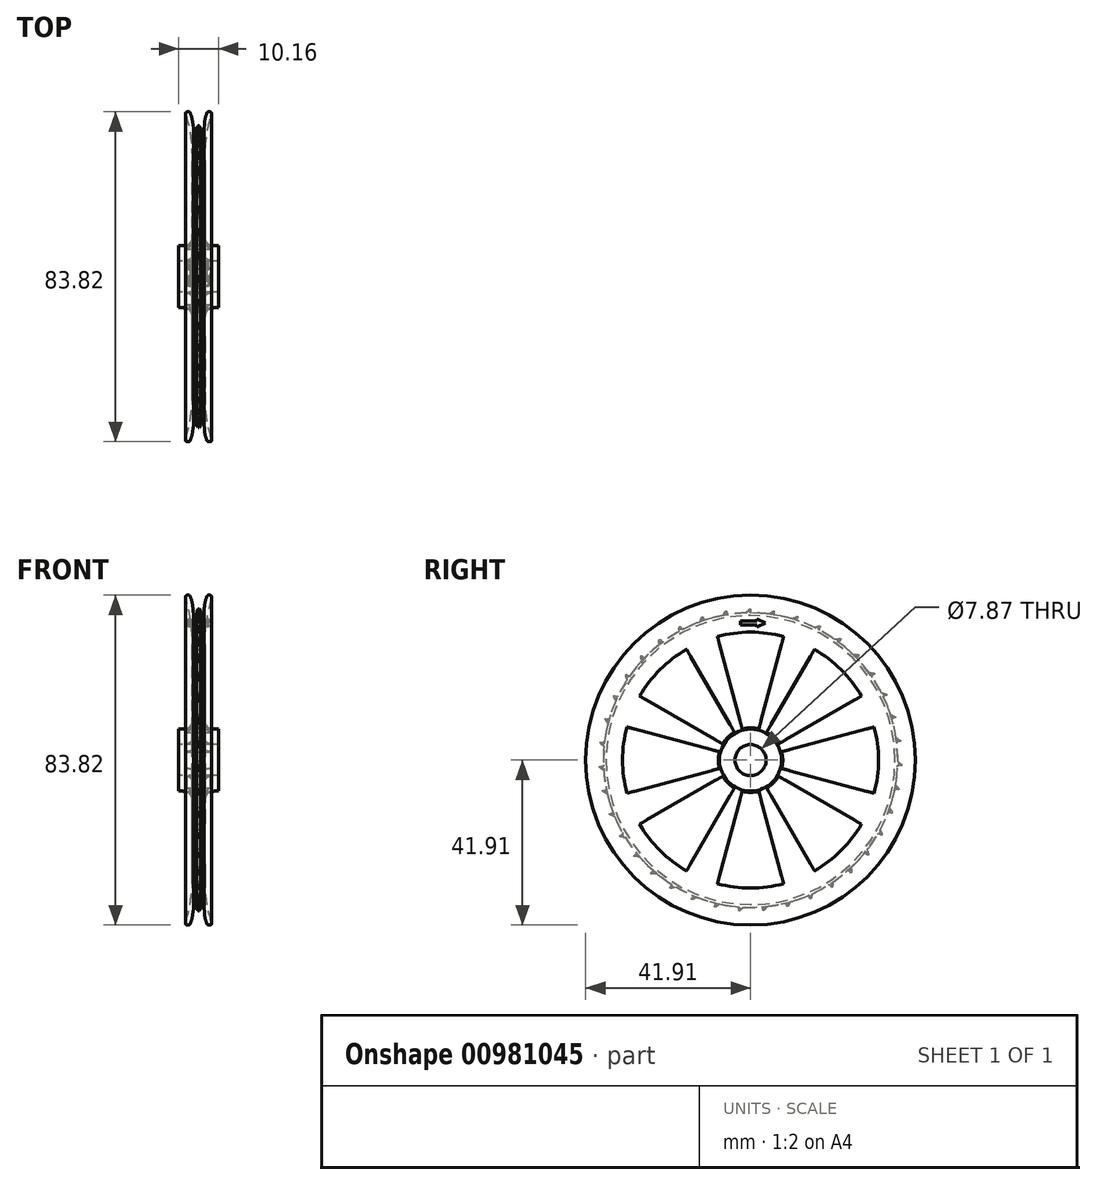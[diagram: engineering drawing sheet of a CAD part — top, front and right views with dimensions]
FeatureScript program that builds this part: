
annotation { "Feature Type Name" : "Feature", "Feature Type Description" : "" }
export const myFeature = defineFeature(function(context is Context, id is Id, definition is map)
    precondition{}
    {
        {
            var Q0;
            Q0=qCreatedBy(makeId("Front.planeOp"),FACE);
            var sketch = newSketch(context, id + "F0", { "sketchPlane" : qUnion([Q0])});
            skLineSegment(sketch, "E0", {"start": v(0, 0) * mm, "end": v(19.05, 0) * mm, "construction": true});
            skLineSegment(sketch, "E1", {"start": v(-5.08, 3.94) * mm, "end": v(0, 3.94) * mm});
            skLineSegment(sketch, "E2", {"start": v(-4.09, 45.93) * mm, "end": v(-2.38, 42.25) * mm});
            skLineSegment(sketch, "E3", {"start": v(0, 45.68) * mm, "end": v(0, -5.83) * mm, "construction": true});
            skPoint(sketch, "E4.visualSharp", {"position": v(0, 36.7) * mm});
            skLineSegment(sketch, "E5", {"start": v(-1.65, 10.41) * mm, "end": v(-1.65, 30.48) * mm});
            skLineSegment(sketch, "E6.trimOffspring", {"start": v(-5.08, 7.87) * mm, "end": v(-5.08, 3.94) * mm});
            skPoint(sketch, "E7.visualSharp", {"position": v(-1.65, 7.87) * mm});
            skLineSegment(sketch, "E8", {"start": v(-1.4, 38.1) * mm, "end": v(-1.46, 38.85) * mm});
            skLineSegment(sketch, "E9", {"start": v(-5.08, 7.87) * mm, "end": v(-4.2, 7.87) * mm});
            skArc(sketch, "E10", {"start": v(-4.09, 45.93) * mm, "mid": v(-4.74, 46.17) * mm, "end": v(-4.98, 45.51) * mm});
            skPoint(sketch, "E11.visualSharp", {"position": v(-1.65, 37.42) * mm});
            skArc(sketch, "E11.filletArc", {"start": v(-1.65, 30.48) * mm, "mid": v(-2.5, 38.18) * mm, "end": v(-4.98, 45.51) * mm});
            skPoint(sketch, "E12.visualSharp", {"position": v(-1.62, 40.63) * mm});
            skArc(sketch, "E12.filletArc", {"start": v(-1.46, 38.85) * mm, "mid": v(-1.77, 40.59) * mm, "end": v(-2.38, 42.25) * mm});
            skPoint(sketch, "E13.visualSharp", {"position": v(-1.4, 38.1) * mm});
            skArc(sketch, "E14.filletArc", {"start": v(-4.2, 7.87) * mm, "mid": v(-2.4, 8.62) * mm, "end": v(-1.65, 10.41) * mm});
            skLineSegment(sketch, "E15.MirrorCS", {"start": v(1.4, 38.1) * mm, "end": v(1.46, 38.85) * mm});
            skLineSegment(sketch, "E16.MirrorCS", {"start": v(5.08, 7.87) * mm, "end": v(4.2, 7.87) * mm});
            skArc(sketch, "E17.MirrorCS", {"start": v(1.46, 38.85) * mm, "mid": v(1.77, 40.59) * mm, "end": v(2.38, 42.25) * mm});
            skArc(sketch, "E18.MirrorCS", {"start": v(4.09, 45.93) * mm, "mid": v(4.74, 46.17) * mm, "end": v(4.98, 45.51) * mm});
            skLineSegment(sketch, "E19.MirrorCS", {"start": v(4.09, 45.93) * mm, "end": v(2.38, 42.25) * mm});
            skArc(sketch, "E20.MirrorCS", {"start": v(4.2, 7.87) * mm, "mid": v(2.4, 8.62) * mm, "end": v(1.65, 10.41) * mm});
            skPoint(sketch, "E21.MirrorP", {"position": v(1.65, 7.87) * mm});
            skPoint(sketch, "E22.MirrorP", {"position": v(1.4, 38.1) * mm});
            skPoint(sketch, "E23.MirrorP", {"position": v(1.65, 37.42) * mm});
            skLineSegment(sketch, "E24.MirrorCS", {"start": v(1.65, 10.41) * mm, "end": v(1.65, 30.48) * mm});
            skLineSegment(sketch, "E25.MirrorCS", {"start": v(5.08, 7.87) * mm, "end": v(5.08, 3.94) * mm});
            skPoint(sketch, "E26.MirrorP", {"position": v(1.62, 40.63) * mm});
            skLineSegment(sketch, "E27.MirrorCS", {"start": v(5.08, 3.94) * mm, "end": v(0, 3.94) * mm});
            skArc(sketch, "E28.MirrorCS", {"start": v(1.65, 30.48) * mm, "mid": v(2.5, 38.18) * mm, "end": v(4.98, 45.51) * mm});
            skLineSegment(sketch, "E29", {"start": v(-0.7, 37.4) * mm, "end": v(0.7, 37.4) * mm});
            skLineSegment(sketch, "E30", {"start": v(-0.7, 37.4) * mm, "end": v(-1.34, 37.4) * mm});
            skLineSegment(sketch, "E31", {"start": v(-1.4, 38.1) * mm, "end": v(-1.34, 37.4) * mm});
            skLineSegment(sketch, "E32.MirrorCS", {"start": v(1.4, 38.1) * mm, "end": v(1.34, 37.4) * mm});
            skLineSegment(sketch, "E33.MirrorCS", {"start": v(0.7, 37.4) * mm, "end": v(1.34, 37.4) * mm});
            skSolve(sketch);
        }
        {
            var Q0;
            Q0=qSketchRegion(id+"F0",true);
            var Q1;
            Q1=sQuery(id+"F0.wireOp",EDGE,"E0");
            revolve(context, id + "F1", {"surfaceOperationType" : NewSurfaceOperationType.NEW, "entities" : qUnion([Q0]), "axis" : qUnion([Q1]), "revolveType" : RevolveType.FULL});
        }
        {
            var Q0;
            Q0=qCreatedBy(makeId("Right.planeOp"),FACE);
            var sketch = newSketch(context, id + "F2", { "sketchPlane" : qUnion([Q0])});
            skArc(sketch, "E34", {"start": v(0, 32.51) * mm, "mid": v(-4.24, 32.23) * mm, "end": v(-8.41, 31.4) * mm});
            skArc(sketch, "E35", {"start": v(0, 8.18) * mm, "mid": v(-1.07, 8.11) * mm, "end": v(-2.12, 7.9) * mm});
            skLineSegment(sketch, "E36", {"start": v(0, 35.5) * mm, "end": v(0, 4.54) * mm, "construction": true});
            skLineSegment(sketch, "E37", {"start": v(-2.12, 7.9) * mm, "end": v(-8.41, 31.4) * mm});
            skArc(sketch, "E38.MirrorCS", {"start": v(0, 32.51) * mm, "mid": v(4.24, 32.23) * mm, "end": v(8.41, 31.4) * mm});
            skLineSegment(sketch, "E39.MirrorCS", {"start": v(2.12, 7.9) * mm, "end": v(8.41, 31.4) * mm});
            skArc(sketch, "E40.MirrorCS", {"start": v(0, 8.18) * mm, "mid": v(1.07, 8.11) * mm, "end": v(2.12, 7.9) * mm});
            skLineSegment(sketch, "E41.1.0", {"start": v(-7.08, 4.1) * mm, "end": v(-28.16, 16.26) * mm});
            skArc(sketch, "E41.1.1", {"start": v(-22.99, 22.99) * mm, "mid": v(-25.8, 19.8) * mm, "end": v(-28.16, 16.26) * mm});
            skArc(sketch, "E41.1.2", {"start": v(-5.78, 5.78) * mm, "mid": v(-6.5, 4.98) * mm, "end": v(-7.08, 4.1) * mm});
            skArc(sketch, "E41.1.3", {"start": v(-5.78, 5.78) * mm, "mid": v(-4.98, 6.5) * mm, "end": v(-4.1, 7.08) * mm});
            skLineSegment(sketch, "E41.1.4", {"start": v(-4.1, 7.08) * mm, "end": v(-16.26, 28.16) * mm});
            skArc(sketch, "E41.1.5", {"start": v(-22.99, 22.99) * mm, "mid": v(-19.8, 25.8) * mm, "end": v(-16.26, 28.16) * mm});
            skLineSegment(sketch, "E41.2.0", {"start": v(-7.9, -2.12) * mm, "end": v(-31.4, -8.41) * mm});
            skArc(sketch, "E41.2.1", {"start": v(-32.51, 0) * mm, "mid": v(-32.23, -4.24) * mm, "end": v(-31.4, -8.41) * mm});
            skArc(sketch, "E41.2.2", {"start": v(-8.18, 0) * mm, "mid": v(-8.11, -1.07) * mm, "end": v(-7.9, -2.12) * mm});
            skArc(sketch, "E41.2.3", {"start": v(-8.18, 0) * mm, "mid": v(-8.11, 1.07) * mm, "end": v(-7.9, 2.12) * mm});
            skLineSegment(sketch, "E41.2.4", {"start": v(-7.9, 2.12) * mm, "end": v(-31.4, 8.41) * mm});
            skArc(sketch, "E41.2.5", {"start": v(-32.51, 0) * mm, "mid": v(-32.23, 4.24) * mm, "end": v(-31.4, 8.41) * mm});
            skLineSegment(sketch, "E42.1.3.0", {"start": v(-4.1, -7.08) * mm, "end": v(-16.26, -28.16) * mm});
            skArc(sketch, "E42.3.3.0", {"start": v(-22.99, -22.99) * mm, "mid": v(-19.8, -25.8) * mm, "end": v(-16.26, -28.16) * mm});
            skArc(sketch, "E42.7.3.0", {"start": v(-5.78, -5.78) * mm, "mid": v(-4.98, -6.5) * mm, "end": v(-4.1, -7.08) * mm});
            skArc(sketch, "E42.11.3.0", {"start": v(-5.78, -5.78) * mm, "mid": v(-6.5, -4.98) * mm, "end": v(-7.08, -4.1) * mm});
            skLineSegment(sketch, "E42.15.3.0", {"start": v(-7.08, -4.1) * mm, "end": v(-28.16, -16.26) * mm});
            skArc(sketch, "E42.18.3.0", {"start": v(-22.99, -22.99) * mm, "mid": v(-25.8, -19.8) * mm, "end": v(-28.16, -16.26) * mm});
            skLineSegment(sketch, "E42.1.4.0", {"start": v(2.12, -7.9) * mm, "end": v(8.41, -31.4) * mm});
            skArc(sketch, "E42.3.4.0", {"start": v(0, -32.51) * mm, "mid": v(4.24, -32.23) * mm, "end": v(8.41, -31.4) * mm});
            skArc(sketch, "E42.7.4.0", {"start": v(0, -8.18) * mm, "mid": v(1.07, -8.11) * mm, "end": v(2.12, -7.9) * mm});
            skArc(sketch, "E42.11.4.0", {"start": v(0, -8.18) * mm, "mid": v(-1.07, -8.11) * mm, "end": v(-2.12, -7.9) * mm});
            skLineSegment(sketch, "E42.15.4.0", {"start": v(-2.12, -7.9) * mm, "end": v(-8.41, -31.4) * mm});
            skArc(sketch, "E42.18.4.0", {"start": v(0, -32.51) * mm, "mid": v(-4.24, -32.23) * mm, "end": v(-8.41, -31.4) * mm});
            skLineSegment(sketch, "E42.1.5.0", {"start": v(7.08, -4.1) * mm, "end": v(28.16, -16.26) * mm});
            skArc(sketch, "E42.3.5.0", {"start": v(22.99, -22.99) * mm, "mid": v(25.8, -19.8) * mm, "end": v(28.16, -16.26) * mm});
            skArc(sketch, "E42.7.5.0", {"start": v(5.78, -5.78) * mm, "mid": v(6.5, -4.98) * mm, "end": v(7.08, -4.1) * mm});
            skArc(sketch, "E42.11.5.0", {"start": v(5.78, -5.78) * mm, "mid": v(4.98, -6.5) * mm, "end": v(4.1, -7.08) * mm});
            skLineSegment(sketch, "E42.15.5.0", {"start": v(4.1, -7.08) * mm, "end": v(16.26, -28.16) * mm});
            skArc(sketch, "E42.18.5.0", {"start": v(22.99, -22.99) * mm, "mid": v(19.8, -25.8) * mm, "end": v(16.26, -28.16) * mm});
            skLineSegment(sketch, "E42.1.6.0", {"start": v(7.9, 2.12) * mm, "end": v(31.4, 8.41) * mm});
            skArc(sketch, "E42.3.6.0", {"start": v(32.51, 0) * mm, "mid": v(32.23, 4.24) * mm, "end": v(31.4, 8.41) * mm});
            skArc(sketch, "E42.7.6.0", {"start": v(8.18, 0) * mm, "mid": v(8.11, 1.07) * mm, "end": v(7.9, 2.12) * mm});
            skArc(sketch, "E42.11.6.0", {"start": v(8.18, 0) * mm, "mid": v(8.11, -1.07) * mm, "end": v(7.9, -2.12) * mm});
            skLineSegment(sketch, "E42.15.6.0", {"start": v(7.9, -2.12) * mm, "end": v(31.4, -8.41) * mm});
            skArc(sketch, "E42.18.6.0", {"start": v(32.51, 0) * mm, "mid": v(32.23, -4.24) * mm, "end": v(31.4, -8.41) * mm});
            skLineSegment(sketch, "E42.1.7.0", {"start": v(4.1, 7.08) * mm, "end": v(16.26, 28.16) * mm});
            skArc(sketch, "E42.3.7.0", {"start": v(22.99, 22.99) * mm, "mid": v(19.8, 25.8) * mm, "end": v(16.26, 28.16) * mm});
            skArc(sketch, "E42.7.7.0", {"start": v(5.78, 5.78) * mm, "mid": v(4.98, 6.5) * mm, "end": v(4.1, 7.08) * mm});
            skArc(sketch, "E42.11.7.0", {"start": v(5.78, 5.78) * mm, "mid": v(6.5, 4.98) * mm, "end": v(7.08, 4.1) * mm});
            skLineSegment(sketch, "E42.15.7.0", {"start": v(7.08, 4.1) * mm, "end": v(28.16, 16.26) * mm});
            skArc(sketch, "E42.18.7.0", {"start": v(22.99, 22.99) * mm, "mid": v(25.8, 19.8) * mm, "end": v(28.16, 16.26) * mm});
            skSolve(sketch);
        }
        {
            var Q0;
            Q0=qSketchRegion(id+"F2",true);
            extrude(context, id + "F3", {"entities" : qUnion([Q0]), "operationType" : NewBodyOperationType.REMOVE, "endBound" : BoundingType.SYMMETRIC, "oppositeDirection" : true, "depth" : 25.4 * mm, "offsetDistance" : 25.4 * mm});
        }
        {
            var Q0;
            Q0=qCreatedBy(makeId("Top.planeOp"),FACE);
            var sketch = newSketch(context, id + "F4", { "sketchPlane" : qUnion([Q0])});
            skLineSegment(sketch, "E43", {"start": v(0, 0) * mm, "end": v(21.6, 0) * mm, "construction": true});
            skSolve(sketch);
        }
        {
            var Q0;
            Q0=qCreatedBy(makeId("Right.planeOp"),FACE);
            var sketch = newSketch(context, id + "F7", { "sketchPlane" : qUnion([Q0])});
            skLineSegment(sketch, "E44", {"start": v(0, 38.35) * mm, "end": v(0, 36.32) * mm});
            skLineSegment(sketch, "E45", {"start": v(0, 36.32) * mm, "end": v(-1.96, 36.32) * mm});
            skLineSegment(sketch, "E46", {"start": v(-1.96, 36.32) * mm, "end": v(-0.25, 38.35) * mm});
            skLineSegment(sketch, "E47", {"start": v(-0.25, 38.35) * mm, "end": v(0, 38.35) * mm});
            skLineSegment(sketch, "E48.1.0", {"start": v(-6.16, 37.86) * mm, "end": v(-5.83, 35.85) * mm});
            skLineSegment(sketch, "E48.1.1", {"start": v(-7.76, 35.54) * mm, "end": v(-6.4, 37.82) * mm});
            skLineSegment(sketch, "E48.1.2", {"start": v(-5.83, 35.85) * mm, "end": v(-7.76, 35.54) * mm});
            skLineSegment(sketch, "E48.1.3", {"start": v(-6.4, 37.82) * mm, "end": v(-6.16, 37.86) * mm});
            skLineSegment(sketch, "E48.2.0", {"start": v(-12.15, 36.38) * mm, "end": v(-11.5, 34.45) * mm});
            skLineSegment(sketch, "E48.2.1", {"start": v(-13.37, 33.83) * mm, "end": v(-12.4, 36.3) * mm});
            skLineSegment(sketch, "E48.2.2", {"start": v(-11.5, 34.45) * mm, "end": v(-13.37, 33.83) * mm});
            skLineSegment(sketch, "E48.2.3", {"start": v(-12.4, 36.3) * mm, "end": v(-12.15, 36.38) * mm});
            skLineSegment(sketch, "E48.3.0", {"start": v(-17.83, 33.96) * mm, "end": v(-16.89, 32.16) * mm});
            skLineSegment(sketch, "E48.3.1", {"start": v(-18.62, 31.25) * mm, "end": v(-18.06, 33.84) * mm});
            skLineSegment(sketch, "E48.3.2", {"start": v(-16.89, 32.16) * mm, "end": v(-18.62, 31.25) * mm});
            skLineSegment(sketch, "E48.3.3", {"start": v(-18.06, 33.84) * mm, "end": v(-17.83, 33.96) * mm});
            skLineSegment(sketch, "E48.4.0", {"start": v(-23.05, 30.65) * mm, "end": v(-21.83, 29.03) * mm});
            skLineSegment(sketch, "E48.4.1", {"start": v(-23.4, 27.85) * mm, "end": v(-23.26, 30.5) * mm});
            skLineSegment(sketch, "E48.4.2", {"start": v(-21.83, 29.03) * mm, "end": v(-23.4, 27.85) * mm});
            skLineSegment(sketch, "E48.4.3", {"start": v(-23.26, 30.5) * mm, "end": v(-23.05, 30.65) * mm});
            skLineSegment(sketch, "E48.5.0", {"start": v(-27.68, 26.55) * mm, "end": v(-26.2, 25.15) * mm});
            skLineSegment(sketch, "E48.5.1", {"start": v(-27.57, 23.73) * mm, "end": v(-27.85, 26.37) * mm});
            skLineSegment(sketch, "E48.5.2", {"start": v(-26.2, 25.15) * mm, "end": v(-27.57, 23.73) * mm});
            skLineSegment(sketch, "E48.5.3", {"start": v(-27.85, 26.37) * mm, "end": v(-27.68, 26.55) * mm});
            skLineSegment(sketch, "E48.6.0", {"start": v(-31.58, 21.77) * mm, "end": v(-29.9, 20.61) * mm});
            skLineSegment(sketch, "E48.6.1", {"start": v(-31.02, 19) * mm, "end": v(-31.72, 21.56) * mm});
            skLineSegment(sketch, "E48.6.2", {"start": v(-29.9, 20.61) * mm, "end": v(-31.02, 19) * mm});
            skLineSegment(sketch, "E48.6.3", {"start": v(-31.72, 21.56) * mm, "end": v(-31.58, 21.77) * mm});
            skLineSegment(sketch, "E48.7.0", {"start": v(-34.66, 16.42) * mm, "end": v(-32.83, 15.55) * mm});
            skLineSegment(sketch, "E48.7.1", {"start": v(-33.67, 13.78) * mm, "end": v(-34.77, 16.19) * mm});
            skLineSegment(sketch, "E48.7.2", {"start": v(-32.83, 15.55) * mm, "end": v(-33.67, 13.78) * mm});
            skLineSegment(sketch, "E48.7.3", {"start": v(-34.77, 16.19) * mm, "end": v(-34.66, 16.42) * mm});
            skLineSegment(sketch, "E48.8.0", {"start": v(-36.85, 10.64) * mm, "end": v(-34.9, 10.08) * mm});
            skLineSegment(sketch, "E48.8.1", {"start": v(-35.44, 8.2) * mm, "end": v(-36.92, 10.4) * mm});
            skLineSegment(sketch, "E48.8.2", {"start": v(-34.9, 10.08) * mm, "end": v(-35.44, 8.2) * mm});
            skLineSegment(sketch, "E48.8.3", {"start": v(-36.92, 10.4) * mm, "end": v(-36.85, 10.64) * mm});
            skLineSegment(sketch, "E48.9.0", {"start": v(-38.08, 4.59) * mm, "end": v(-36.06, 4.34) * mm});
            skLineSegment(sketch, "E48.9.1", {"start": v(-36.3, 2.4) * mm, "end": v(-38.1, 4.33) * mm});
            skLineSegment(sketch, "E48.9.2", {"start": v(-36.06, 4.34) * mm, "end": v(-36.3, 2.4) * mm});
            skLineSegment(sketch, "E48.9.3", {"start": v(-38.1, 4.33) * mm, "end": v(-38.08, 4.59) * mm});
            skLineSegment(sketch, "E48.10.0", {"start": v(-38.32, -1.58) * mm, "end": v(-36.3, -1.5) * mm});
            skLineSegment(sketch, "E48.10.1", {"start": v(-36.21, -3.46) * mm, "end": v(-38.31, -1.84) * mm});
            skLineSegment(sketch, "E48.10.2", {"start": v(-36.3, -1.5) * mm, "end": v(-36.21, -3.46) * mm});
            skLineSegment(sketch, "E48.10.3", {"start": v(-38.31, -1.84) * mm, "end": v(-38.32, -1.58) * mm});
            skLineSegment(sketch, "E48.11.0", {"start": v(-37.57, -7.72) * mm, "end": v(-35.58, -7.3) * mm});
            skLineSegment(sketch, "E48.11.1", {"start": v(-35.19, -9.23) * mm, "end": v(-37.52, -7.96) * mm});
            skLineSegment(sketch, "E48.11.2", {"start": v(-35.58, -7.3) * mm, "end": v(-35.19, -9.23) * mm});
            skLineSegment(sketch, "E48.11.3", {"start": v(-37.52, -7.96) * mm, "end": v(-37.57, -7.72) * mm});
            skLineSegment(sketch, "E48.12.0", {"start": v(-35.84, -13.65) * mm, "end": v(-33.95, -12.92) * mm});
            skLineSegment(sketch, "E48.12.1", {"start": v(-33.25, -14.75) * mm, "end": v(-35.75, -13.88) * mm});
            skLineSegment(sketch, "E48.12.2", {"start": v(-33.95, -12.92) * mm, "end": v(-33.25, -14.75) * mm});
            skLineSegment(sketch, "E48.12.3", {"start": v(-35.75, -13.88) * mm, "end": v(-35.84, -13.65) * mm});
            skLineSegment(sketch, "E48.13.0", {"start": v(-33.19, -19.22) * mm, "end": v(-31.43, -18.2) * mm});
            skLineSegment(sketch, "E48.13.1", {"start": v(-30.45, -19.9) * mm, "end": v(-33.06, -19.44) * mm});
            skLineSegment(sketch, "E48.13.2", {"start": v(-31.43, -18.2) * mm, "end": v(-30.45, -19.9) * mm});
            skLineSegment(sketch, "E48.13.3", {"start": v(-33.06, -19.44) * mm, "end": v(-33.19, -19.22) * mm});
            skLineSegment(sketch, "E48.14.0", {"start": v(-29.67, -24.3) * mm, "end": v(-28.1, -23.01) * mm});
            skLineSegment(sketch, "E48.14.1", {"start": v(-26.86, -24.53) * mm, "end": v(-29.51, -24.5) * mm});
            skLineSegment(sketch, "E48.14.2", {"start": v(-28.1, -23.01) * mm, "end": v(-26.86, -24.53) * mm});
            skLineSegment(sketch, "E48.14.3", {"start": v(-29.51, -24.5) * mm, "end": v(-29.67, -24.3) * mm});
            skLineSegment(sketch, "E48.15.0", {"start": v(-25.39, -28.75) * mm, "end": v(-24.04, -27.23) * mm});
            skLineSegment(sketch, "E48.15.1", {"start": v(-22.57, -28.52) * mm, "end": v(-25.2, -28.92) * mm});
            skLineSegment(sketch, "E48.15.2", {"start": v(-24.04, -27.23) * mm, "end": v(-22.57, -28.52) * mm});
            skLineSegment(sketch, "E48.15.3", {"start": v(-25.2, -28.92) * mm, "end": v(-25.39, -28.75) * mm});
            skLineSegment(sketch, "E48.16.0", {"start": v(-20.44, -32.45) * mm, "end": v(-19.36, -30.73) * mm});
            skLineSegment(sketch, "E48.16.1", {"start": v(-17.7, -31.78) * mm, "end": v(-20.23, -32.59) * mm});
            skLineSegment(sketch, "E48.16.2", {"start": v(-19.36, -30.73) * mm, "end": v(-17.7, -31.78) * mm});
            skLineSegment(sketch, "E48.16.3", {"start": v(-20.23, -32.59) * mm, "end": v(-20.44, -32.45) * mm});
            skLineSegment(sketch, "E48.17.0", {"start": v(-14.97, -35.31) * mm, "end": v(-14.18, -33.44) * mm});
            skLineSegment(sketch, "E48.17.1", {"start": v(-12.37, -34.2) * mm, "end": v(-14.74, -35.41) * mm});
            skLineSegment(sketch, "E48.17.2", {"start": v(-14.18, -33.44) * mm, "end": v(-12.37, -34.2) * mm});
            skLineSegment(sketch, "E48.17.3", {"start": v(-14.74, -35.41) * mm, "end": v(-14.97, -35.31) * mm});
            skLineSegment(sketch, "E48.18.0", {"start": v(-9.1, -37.26) * mm, "end": v(-8.63, -35.28) * mm});
            skLineSegment(sketch, "E48.18.1", {"start": v(-6.72, -35.75) * mm, "end": v(-8.86, -37.32) * mm});
            skLineSegment(sketch, "E48.18.2", {"start": v(-8.63, -35.28) * mm, "end": v(-6.72, -35.75) * mm});
            skLineSegment(sketch, "E48.18.3", {"start": v(-8.86, -37.32) * mm, "end": v(-9.1, -37.26) * mm});
            skLineSegment(sketch, "E48.19.0", {"start": v(-3, -38.24) * mm, "end": v(-2.85, -36.21) * mm});
            skLineSegment(sketch, "E48.19.1", {"start": v(-0.9, -36.36) * mm, "end": v(-2.76, -38.26) * mm});
            skLineSegment(sketch, "E48.19.2", {"start": v(-2.85, -36.21) * mm, "end": v(-0.9, -36.36) * mm});
            skLineSegment(sketch, "E48.19.3", {"start": v(-2.76, -38.26) * mm, "end": v(-3, -38.24) * mm});
            skLineSegment(sketch, "E48.20.0", {"start": v(3.17, -38.22) * mm, "end": v(3, -36.2) * mm});
            skLineSegment(sketch, "E48.20.1", {"start": v(4.95, -36.04) * mm, "end": v(3.42, -38.2) * mm});
            skLineSegment(sketch, "E48.20.2", {"start": v(3, -36.2) * mm, "end": v(4.95, -36.04) * mm});
            skLineSegment(sketch, "E48.20.3", {"start": v(3.42, -38.2) * mm, "end": v(3.17, -38.22) * mm});
            skLineSegment(sketch, "E48.21.0", {"start": v(9.26, -37.22) * mm, "end": v(8.77, -35.25) * mm});
            skLineSegment(sketch, "E48.21.1", {"start": v(10.67, -34.77) * mm, "end": v(9.5, -37.16) * mm});
            skLineSegment(sketch, "E48.21.2", {"start": v(8.77, -35.25) * mm, "end": v(10.67, -34.77) * mm});
            skLineSegment(sketch, "E48.21.3", {"start": v(9.5, -37.16) * mm, "end": v(9.26, -37.22) * mm});
            skLineSegment(sketch, "E48.22.0", {"start": v(15.12, -35.25) * mm, "end": v(14.31, -33.38) * mm});
            skLineSegment(sketch, "E48.22.1", {"start": v(16.12, -32.61) * mm, "end": v(15.35, -35.15) * mm});
            skLineSegment(sketch, "E48.22.2", {"start": v(14.31, -33.38) * mm, "end": v(16.12, -32.61) * mm});
            skLineSegment(sketch, "E48.22.3", {"start": v(15.35, -35.15) * mm, "end": v(15.12, -35.25) * mm});
            skLineSegment(sketch, "E48.23.0", {"start": v(20.58, -32.37) * mm, "end": v(19.49, -30.65) * mm});
            skLineSegment(sketch, "E48.23.1", {"start": v(21.14, -29.6) * mm, "end": v(20.8, -32.23) * mm});
            skLineSegment(sketch, "E48.23.2", {"start": v(19.49, -30.65) * mm, "end": v(21.14, -29.6) * mm});
            skLineSegment(sketch, "E48.23.3", {"start": v(20.8, -32.23) * mm, "end": v(20.58, -32.37) * mm});
            skLineSegment(sketch, "E48.24.0", {"start": v(25.5, -28.64) * mm, "end": v(24.16, -27.13) * mm});
            skLineSegment(sketch, "E48.24.1", {"start": v(25.62, -25.82) * mm, "end": v(25.7, -28.47) * mm});
            skLineSegment(sketch, "E48.24.2", {"start": v(24.16, -27.13) * mm, "end": v(25.62, -25.82) * mm});
            skLineSegment(sketch, "E48.24.3", {"start": v(25.7, -28.47) * mm, "end": v(25.5, -28.64) * mm});
            skLineSegment(sketch, "E48.25.0", {"start": v(29.77, -24.18) * mm, "end": v(28.2, -22.9) * mm});
            skLineSegment(sketch, "E48.25.1", {"start": v(29.43, -21.38) * mm, "end": v(29.93, -23.98) * mm});
            skLineSegment(sketch, "E48.25.2", {"start": v(28.2, -22.9) * mm, "end": v(29.43, -21.38) * mm});
            skLineSegment(sketch, "E48.25.3", {"start": v(29.93, -23.98) * mm, "end": v(29.77, -24.18) * mm});
            skLineSegment(sketch, "E48.26.0", {"start": v(33.27, -19.09) * mm, "end": v(31.5, -18.07) * mm});
            skLineSegment(sketch, "E48.26.1", {"start": v(32.48, -16.37) * mm, "end": v(33.4, -18.87) * mm});
            skLineSegment(sketch, "E48.26.2", {"start": v(31.5, -18.07) * mm, "end": v(32.48, -16.37) * mm});
            skLineSegment(sketch, "E48.26.3", {"start": v(33.4, -18.87) * mm, "end": v(33.27, -19.09) * mm});
            skLineSegment(sketch, "E48.27.0", {"start": v(35.9, -13.5) * mm, "end": v(34, -12.78) * mm});
            skLineSegment(sketch, "E48.27.1", {"start": v(34.69, -10.95) * mm, "end": v(35.99, -13.26) * mm});
            skLineSegment(sketch, "E48.27.2", {"start": v(34, -12.78) * mm, "end": v(34.69, -10.95) * mm});
            skLineSegment(sketch, "E48.27.3", {"start": v(35.99, -13.26) * mm, "end": v(35.9, -13.5) * mm});
            skLineSegment(sketch, "E48.28.0", {"start": v(37.6, -7.56) * mm, "end": v(35.6, -7.16) * mm});
            skLineSegment(sketch, "E48.28.1", {"start": v(36, -5.24) * mm, "end": v(37.65, -7.31) * mm});
            skLineSegment(sketch, "E48.28.2", {"start": v(35.6, -7.16) * mm, "end": v(36, -5.24) * mm});
            skLineSegment(sketch, "E48.28.3", {"start": v(37.65, -7.31) * mm, "end": v(37.6, -7.56) * mm});
            skPoint(sketch, "E48.center", {"position": v(0, 0) * mm});
            skLineSegment(sketch, "E48.anchor1", {"start": v(0, 0) * mm, "end": v(-1.96, 36.32) * mm, "construction": true});
            skLineSegment(sketch, "E48.anchor2", {"start": v(0, 0) * mm, "end": v(3.75, 36.18) * mm, "construction": true});
            skLineSegment(sketch, "E49.3.29.0", {"start": v(36.37, 0.6) * mm, "end": v(38.34, -1.17) * mm});
            skLineSegment(sketch, "E49.4.29.0", {"start": v(38.33, -1.43) * mm, "end": v(36.3, -1.35) * mm});
            skLineSegment(sketch, "E49.6.29.0", {"start": v(36.3, -1.35) * mm, "end": v(36.37, 0.6) * mm});
            skLineSegment(sketch, "E49.9.29.0", {"start": v(38.34, -1.17) * mm, "end": v(38.33, -1.43) * mm});
            skLineSegment(sketch, "E49.3.30.0", {"start": v(35.8, 6.44) * mm, "end": v(38.03, 5) * mm});
            skLineSegment(sketch, "E49.4.30.0", {"start": v(38.06, 4.74) * mm, "end": v(36.04, 4.5) * mm});
            skLineSegment(sketch, "E49.6.30.0", {"start": v(36.04, 4.5) * mm, "end": v(35.8, 6.44) * mm});
            skLineSegment(sketch, "E49.9.30.0", {"start": v(38.03, 5) * mm, "end": v(38.06, 4.74) * mm});
            skLineSegment(sketch, "E49.3.31.0", {"start": v(34.3, 12.1) * mm, "end": v(36.73, 11.04) * mm});
            skLineSegment(sketch, "E49.4.31.0", {"start": v(36.8, 10.8) * mm, "end": v(34.85, 10.22) * mm});
            skLineSegment(sketch, "E49.6.31.0", {"start": v(34.85, 10.22) * mm, "end": v(34.3, 12.1) * mm});
            skLineSegment(sketch, "E49.9.31.0", {"start": v(36.73, 11.04) * mm, "end": v(36.8, 10.8) * mm});
            skLineSegment(sketch, "E49.3.32.0", {"start": v(31.92, 17.45) * mm, "end": v(34.49, 16.79) * mm});
            skLineSegment(sketch, "E49.4.32.0", {"start": v(34.6, 16.56) * mm, "end": v(32.76, 15.68) * mm});
            skLineSegment(sketch, "E49.6.32.0", {"start": v(32.76, 15.68) * mm, "end": v(31.92, 17.45) * mm});
            skLineSegment(sketch, "E49.9.32.0", {"start": v(34.49, 16.79) * mm, "end": v(34.6, 16.56) * mm});
            skLineSegment(sketch, "E49.3.33.0", {"start": v(28.7, 22.35) * mm, "end": v(31.34, 22.1) * mm});
            skLineSegment(sketch, "E49.4.33.0", {"start": v(31.49, 21.9) * mm, "end": v(29.82, 20.74) * mm});
            skLineSegment(sketch, "E49.6.33.0", {"start": v(29.82, 20.74) * mm, "end": v(28.7, 22.35) * mm});
            skLineSegment(sketch, "E49.9.33.0", {"start": v(31.34, 22.1) * mm, "end": v(31.49, 21.9) * mm});
            skLineSegment(sketch, "E49.3.34.0", {"start": v(24.74, 26.66) * mm, "end": v(27.39, 26.85) * mm});
            skLineSegment(sketch, "E49.4.34.0", {"start": v(27.57, 26.67) * mm, "end": v(26.1, 25.26) * mm});
            skLineSegment(sketch, "E49.6.34.0", {"start": v(26.1, 25.26) * mm, "end": v(24.74, 26.66) * mm});
            skLineSegment(sketch, "E49.9.34.0", {"start": v(27.39, 26.85) * mm, "end": v(27.57, 26.67) * mm});
            skLineSegment(sketch, "E49.3.35.0", {"start": v(20.14, 30.29) * mm, "end": v(22.72, 30.9) * mm});
            skLineSegment(sketch, "E49.4.35.0", {"start": v(22.93, 30.75) * mm, "end": v(21.71, 29.12) * mm});
            skLineSegment(sketch, "E49.6.35.0", {"start": v(21.71, 29.12) * mm, "end": v(20.14, 30.29) * mm});
            skLineSegment(sketch, "E49.9.35.0", {"start": v(22.72, 30.9) * mm, "end": v(22.93, 30.75) * mm});
            skLineSegment(sketch, "E49.3.36.0", {"start": v(15.02, 33.13) * mm, "end": v(17.47, 34.15) * mm});
            skLineSegment(sketch, "E49.4.36.0", {"start": v(17.7, 34.03) * mm, "end": v(16.76, 32.23) * mm});
            skLineSegment(sketch, "E49.6.36.0", {"start": v(16.76, 32.23) * mm, "end": v(15.02, 33.13) * mm});
            skLineSegment(sketch, "E49.9.36.0", {"start": v(17.47, 34.15) * mm, "end": v(17.7, 34.03) * mm});
            skLineSegment(sketch, "E49.3.37.0", {"start": v(9.5, 35.11) * mm, "end": v(11.76, 36.5) * mm});
            skLineSegment(sketch, "E49.4.37.0", {"start": v(12, 36.43) * mm, "end": v(11.37, 34.5) * mm});
            skLineSegment(sketch, "E49.6.37.0", {"start": v(11.37, 34.5) * mm, "end": v(9.5, 35.11) * mm});
            skLineSegment(sketch, "E49.9.37.0", {"start": v(11.76, 36.5) * mm, "end": v(12, 36.43) * mm});
            skLineSegment(sketch, "E49.3.38.0", {"start": v(3.75, 36.18) * mm, "end": v(5.75, 37.92) * mm});
            skLineSegment(sketch, "E49.4.38.0", {"start": v(6, 37.88) * mm, "end": v(5.68, 35.87) * mm});
            skLineSegment(sketch, "E49.6.38.0", {"start": v(5.68, 35.87) * mm, "end": v(3.75, 36.18) * mm});
            skLineSegment(sketch, "E49.9.38.0", {"start": v(5.75, 37.92) * mm, "end": v(6, 37.88) * mm});
            skSolve(sketch);
        }
        {
            var Q0;
            Q0=qSketchRegion(id+"F7",true);
            extrude(context, id + "F8", {"entities" : qUnion([Q0]), "operationType" : NewBodyOperationType.ADD, "endBound" : BoundingType.SYMMETRIC, "depth" : 0.89 * mm, "offsetDistance" : 25.4 * mm});
        }
        {
            var Q0;
            Q0=qCreatedBy(makeId("Front.planeOp"),FACE);
            var sketch = newSketch(context, id + "F9", { "sketchPlane" : qUnion([Q0])});
            skLineSegment(sketch, "E50", {"start": v(0, 38.64) * mm, "end": v(0, 37.7) * mm, "construction": true});
            skLineSegment(sketch, "E51", {"start": v(-0.5, 37.6) * mm, "end": v(-0.08, 38.48) * mm});
            skLineSegment(sketch, "E52", {"start": v(-0.5, 37.6) * mm, "end": v(-0.82, 38.64) * mm});
            skLineSegment(sketch, "E53", {"start": v(-0.82, 38.64) * mm, "end": v(0, 38.64) * mm});
            skLineSegment(sketch, "E54.MirrorCS", {"start": v(0.5, 37.6) * mm, "end": v(0.08, 38.48) * mm});
            skLineSegment(sketch, "E55.MirrorCS", {"start": v(0.5, 37.6) * mm, "end": v(0.82, 38.64) * mm});
            skLineSegment(sketch, "E56.MirrorCS", {"start": v(0.82, 38.64) * mm, "end": v(0, 38.64) * mm});
            skLineSegment(sketch, "E57", {"start": v(-0.08, 38.48) * mm, "end": v(0.08, 38.48) * mm});
            skPoint(sketch, "E58.orphan", {"position": v(0, 38.64) * mm});
            skSolve(sketch);
        }
        {
            var Q0;
            Q0=qCreatedBy(makeId("Right.planeOp"),FACE);
            var sketch = newSketch(context, id + "F10", { "sketchPlane" : qUnion([Q0])});
            skLineSegment(sketch, "E59", {"start": v(-3.44, 34.82) * mm, "end": v(3.76, 34.82) * mm, "construction": true});
            skLineSegment(sketch, "E60", {"start": v(-2.56, 34.82) * mm, "end": v(-2.56, 34.3) * mm});
            skLineSegment(sketch, "E61", {"start": v(-2.56, 34.3) * mm, "end": v(1.68, 34.3) * mm});
            skLineSegment(sketch, "E62", {"start": v(1.68, 34.3) * mm, "end": v(1.68, 33.79) * mm});
            skLineSegment(sketch, "E63", {"start": v(1.68, 33.79) * mm, "end": v(3.76, 34.82) * mm});
            skLineSegment(sketch, "E64.MirrorCS", {"start": v(1.68, 35.33) * mm, "end": v(1.68, 35.85) * mm});
            skLineSegment(sketch, "E65.MirrorCS", {"start": v(-2.56, 34.82) * mm, "end": v(-2.56, 35.33) * mm});
            skLineSegment(sketch, "E66.MirrorCS", {"start": v(-2.56, 35.33) * mm, "end": v(1.68, 35.33) * mm});
            skLineSegment(sketch, "E67.MirrorCS", {"start": v(1.68, 35.85) * mm, "end": v(3.76, 34.82) * mm});
            skSolve(sketch);
        }
        {
            var Q0;
            Q0=qSketchRegion(id+"F10",true);
            extrude(context, id + "F11", {"entities" : qUnion([Q0]), "operationType" : NewBodyOperationType.ADD, "endBound" : BoundingType.SYMMETRIC, "depth" : 5.08 * mm, "offsetDistance" : 25.4 * mm});
        }
        {
            var Q0;
            Q0=qCreatedBy(makeId("Front.planeOp"),FACE);
            var sketch = newSketch(context, id + "F12", { "sketchPlane" : qUnion([Q0])});
            skLineSegment(sketch, "E68.bottom", {"start": v(-6.18, 49.12) * mm, "end": v(-1.33, 49.12) * mm});
            skLineSegment(sketch, "E68.top", {"start": v(-6.18, 43.18) * mm, "end": v(-1.33, 43.18) * mm});
            skLineSegment(sketch, "E68.left", {"start": v(-6.18, 49.12) * mm, "end": v(-6.18, 43.18) * mm});
            skLineSegment(sketch, "E68.right", {"start": v(-1.33, 49.12) * mm, "end": v(-1.33, 43.18) * mm});
            skSolve(sketch);
        }
        {
            var Q0;
            Q0=qSketchRegion(id+"F12",true);
            var Q1;
            Q1=sQuery(id+"F4.wireOp",EDGE,"E43");
            revolve(context, id + "F13", {"operationType" : NewBodyOperationType.REMOVE, "surfaceOperationType" : NewSurfaceOperationType.NEW, "entities" : qUnion([Q0]), "axis" : qUnion([Q1]), "revolveType" : RevolveType.FULL, "oppositeDirection" : true});
        }
        {
            var Q0;
            Q0=qSketchRegion(id+"F9",true);
            var Q1;
            Q1=sQuery(id+"F4.wireOp",EDGE,"E43");
            revolve(context, id + "F14", {"operationType" : NewBodyOperationType.REMOVE, "surfaceOperationType" : NewSurfaceOperationType.NEW, "entities" : qUnion([Q0]), "axis" : qUnion([Q1]), "revolveType" : RevolveType.FULL, "oppositeDirection" : true});
        }
        {
            var Q0;
            Q0=makeQuery(id+"F13.boolean.opBoolean","INTERSECT",EDGE,{"derivedFrom":[makeQuery(id+"F1.opRevolve","SWEPT_FACE",FACE,{"disambiguationData":[OSD([sQuery(id+"F0.wireOp",EDGE,"E11.filletArc")])]}),makeQuery(id+"F13.opRevolve","SWEPT_FACE",FACE,{"disambiguationData":[OSD([sQuery(id+"F12.wireOp",EDGE,"E68.top")])]})]});
            var Q1;
            Q1=makeQuery(id+"F13.boolean.opBoolean","INTERSECT",EDGE,{"derivedFrom":[makeQuery(id+"F1.opRevolve","SWEPT_FACE",FACE,{"disambiguationData":[OSD([sQuery(id+"F0.wireOp",EDGE,"E2")])]}),makeQuery(id+"F13.opRevolve","SWEPT_FACE",FACE,{"disambiguationData":[OSD([sQuery(id+"F12.wireOp",EDGE,"E68.top")])]})]});
            fillet(context, id + "F15", {"entities" : qUnion([Q0, Q1]), "radius" : 0.5 * mm, "tangentPropagation" : true, "allowEdgeOverflow" : false});
        }
        {
            var Q0;
            Q0=qCreatedBy(makeId("Front.planeOp"),FACE);
            var sketch = newSketch(context, id + "F16", { "sketchPlane" : qUnion([Q0])});
            skLineSegment(sketch, "E69", {"start": v(-0.45, 37.77) * mm, "end": v(-0.45, 36.97) * mm});
            skLineSegment(sketch, "E70", {"start": v(-0.7, 36.71) * mm, "end": v(-1.08, 36.71) * mm});
            skLineSegment(sketch, "E71", {"start": v(-1.33, 36.97) * mm, "end": v(-1.33, 37.77) * mm});
            skLineSegment(sketch, "E72", {"start": v(0, 39.2) * mm, "end": v(0, 36.3) * mm, "construction": true});
            skLineSegment(sketch, "E73.MirrorCS", {"start": v(0.45, 37.77) * mm, "end": v(0.45, 36.97) * mm});
            skLineSegment(sketch, "E74.MirrorCS", {"start": v(0.7, 36.71) * mm, "end": v(1.08, 36.71) * mm});
            skLineSegment(sketch, "E75.MirrorCS", {"start": v(1.33, 36.97) * mm, "end": v(1.33, 37.77) * mm});
            skLineSegment(sketch, "E76", {"start": v(-1.33, 37.77) * mm, "end": v(-0.45, 37.77) * mm});
            skPoint(sketch, "E77.orphan", {"position": v(-0.45, 37.94) * mm});
            skLineSegment(sketch, "E78.MirrorCS", {"start": v(1.33, 37.77) * mm, "end": v(0.45, 37.77) * mm});
            skPoint(sketch, "E79.orphan", {"position": v(0.45, 37.94) * mm});
            skPoint(sketch, "E80.MirrorCS.start.orphan", {"position": v(1.33, 37.77) * mm});
            skPoint(sketch, "E81.visualSharp", {"position": v(-1.33, 36.71) * mm});
            skArc(sketch, "E81.filletArc", {"start": v(-1.33, 36.97) * mm, "mid": v(-1.26, 36.79) * mm, "end": v(-1.08, 36.71) * mm});
            skPoint(sketch, "E82.visualSharp", {"position": v(1.33, 36.71) * mm});
            skArc(sketch, "E82.filletArc", {"start": v(1.08, 36.71) * mm, "mid": v(1.26, 36.79) * mm, "end": v(1.33, 36.97) * mm});
            skPoint(sketch, "E83.visualSharp", {"position": v(-0.45, 36.71) * mm});
            skArc(sketch, "E83.filletArc", {"start": v(-0.7, 36.71) * mm, "mid": v(-0.52, 36.79) * mm, "end": v(-0.45, 36.97) * mm});
            skPoint(sketch, "E84.visualSharp", {"position": v(0.45, 36.71) * mm});
            skArc(sketch, "E84.filletArc", {"start": v(0.45, 36.97) * mm, "mid": v(0.52, 36.79) * mm, "end": v(0.7, 36.71) * mm});
            skSolve(sketch);
        }
        {
            var Q0;
            Q0=qSketchRegion(id+"F16",true);
            var Q1;
            Q1=sQuery(id+"F4.wireOp",EDGE,"E43");
            revolve(context, id + "F17", {"operationType" : NewBodyOperationType.REMOVE, "surfaceOperationType" : NewSurfaceOperationType.NEW, "entities" : qUnion([Q0]), "axis" : qUnion([Q1]), "revolveType" : RevolveType.FULL, "oppositeDirection" : true});
        }
        {
            var Q0;
            Q0=makeQuery(id+"F17.boolean.opBoolean","INTERSECT",EDGE,{"derivedFrom":[makeQuery(id+"F1.opRevolve","SWEPT_FACE",FACE,{"disambiguationData":[OSD([sQuery(id+"F0.wireOp",EDGE,"E29"),sQuery(id+"F0.wireOp",EDGE,"E30"),sQuery(id+"F0.wireOp",EDGE,"E33.MirrorCS")])]}),makeQuery(id+"F17.opRevolve","SWEPT_FACE",FACE,{"disambiguationData":[OSD([sQuery(id+"F16.wireOp",EDGE,"E71")])]})]});
            var Q1;
            Q1=makeQuery(id+"F17.boolean.opBoolean","INTERSECT",EDGE,{"derivedFrom":[makeQuery(id+"F1.opRevolve","SWEPT_FACE",FACE,{"disambiguationData":[OSD([sQuery(id+"F0.wireOp",EDGE,"E29"),sQuery(id+"F0.wireOp",EDGE,"E30"),sQuery(id+"F0.wireOp",EDGE,"E33.MirrorCS")])]}),makeQuery(id+"F17.opRevolve","SWEPT_FACE",FACE,{"disambiguationData":[OSD([sQuery(id+"F16.wireOp",EDGE,"E75.MirrorCS")])]})]});
            fillet(context, id + "F18", {"entities" : qUnion([Q0, Q1]), "radius" : 2.54 * mm, "tangentPropagation" : true, "allowEdgeOverflow" : false});
        }
        {
            var Q0;
            Q0=qCreatedBy(makeId("Right.planeOp"),FACE);
            var sketch = newSketch(context, id + "F19", { "sketchPlane" : qUnion([Q0])});
            skCircle(sketch, "E85", {"center": v(0, 0) * mm, "radius": 41.91 * mm});
            skCircle(sketch, "E86", {"center": v(0, 0) * mm, "radius": 53.58 * mm});
            skSolve(sketch);
        }
        {
            var Q0;
            Q0=qSketchRegion(id+"F19",true);
            extrude(context, id + "F20", {"entities" : qUnion([Q0]), "operationType" : NewBodyOperationType.REMOVE, "endBound" : BoundingType.SYMMETRIC, "oppositeDirection" : true, "depth" : 25.4 * mm, "offsetDistance" : 25.4 * mm});
        }
        {
            var Q0;
            Q0=makeQuery(id+"F20.boolean.opBoolean","INTERSECT",EDGE,{"derivedFrom":[makeQuery(id+"F1.opRevolve","SWEPT_FACE",FACE,{"disambiguationData":[OSD([sQuery(id+"F0.wireOp",EDGE,"E17.MirrorCS")])]}),makeQuery(id+"F20.opExtrude","SWEPT_FACE",FACE,{"disambiguationData":[OSD([sQuery(id+"F19.wireOp",EDGE,"E85")])]})]});
            var Q1;
            Q1=makeQuery(id+"F20.boolean.opBoolean","INTERSECT",EDGE,{"derivedFrom":[makeQuery(id+"F1.opRevolve","SWEPT_FACE",FACE,{"disambiguationData":[OSD([sQuery(id+"F0.wireOp",EDGE,"E28.MirrorCS")])]}),makeQuery(id+"F20.opExtrude","SWEPT_FACE",FACE,{"disambiguationData":[OSD([sQuery(id+"F19.wireOp",EDGE,"E85")])]})]});
            var Q2;
            Q2=makeQuery(id+"F20.boolean.opBoolean","INTERSECT",EDGE,{"derivedFrom":[makeQuery(id+"F1.opRevolve","SWEPT_FACE",FACE,{"disambiguationData":[OSD([sQuery(id+"F0.wireOp",EDGE,"E12.filletArc")])]}),makeQuery(id+"F20.opExtrude","SWEPT_FACE",FACE,{"disambiguationData":[OSD([sQuery(id+"F19.wireOp",EDGE,"E85")])]})]});
            var Q3;
            Q3=makeQuery(id+"F20.boolean.opBoolean","INTERSECT",EDGE,{"derivedFrom":[makeQuery(id+"F1.opRevolve","SWEPT_FACE",FACE,{"disambiguationData":[OSD([sQuery(id+"F0.wireOp",EDGE,"E11.filletArc")])]}),makeQuery(id+"F20.opExtrude","SWEPT_FACE",FACE,{"disambiguationData":[OSD([sQuery(id+"F19.wireOp",EDGE,"E85")])]})]});
            fillet(context, id + "F21", {"entities" : qUnion([Q0, Q1, Q2, Q3]), "radius" : 0.5 * mm, "tangentPropagation" : true, "allowEdgeOverflow" : false});
        }
    });
